# Revit family: RHTG1025
name_source: partatom
category: Windows
units: mm (PartAtom-declared; Revit-internal decimal feet)

## family parameters
Always vertical = No
Cut with Voids When Loaded = No
Host = Roof
Room Calculation Point = No
Shared = No

## types (4) — shared parameters
A = 1000 mm  [stored 3.28084 ft]
Analytic Construction = <None>
BEV L 1 = 400 mm  [stored 1.31234 ft]
BEV L 3 = 400 mm  [stored 1.31234 ft]
Define Thermal Properties by = Schematic Type
Geluidwerendheid = 27 dB
Hatch Material = Gorter
Manufacturer = Gorter
Model = RHTG
Oppervlaktebehandeling binnenzijde = Gepoedercoat RAL9010
Gepoedercoat in RAL7011 (buitenzijde) en RAL9010 (binnenzijde).
Gepoedercoat RAL 9010
Oppervlaktebehandeling buitenzijde = Gepoedercoat RAL9005 / RAL9010
Gepoedercoat in RAL7011 (buitenzijde) en RAL9010 (binnenzijde).
Gepoedercoat RAL 7011
Rough Width = 1000 mm  [stored 3.28084 ft]
URL = https://www.gortergroup.com
Width = 1000 mm  [stored 3.28084 ft]

## per-type parameters (varying)
| type | B | BEV L 2 | Height | Rough Height | Weight (kg) |
| RHTG1015 | 1500 mm  [stored 4.92126 ft] | 400 mm  [stored 1.31234 ft] | 1500 mm  [stored 4.92126 ft] | 1500 mm  [stored 4.92126 ft] | 173 |
| RHTG1025 | 2500 mm  [stored 8.2021 ft] | 800 mm  [stored 2.62467 ft] | 2500 mm  [stored 8.2021 ft] | 2500 mm  [stored 8.2021 ft] | 264 |
| RHTG1030 | 3000 mm  [stored 9.84252 ft] | 400 mm  [stored 1.31234 ft] | 3000 mm  [stored 9.84252 ft] | 3000 mm  [stored 9.84252 ft] | 309 |
| RHTG1020 | 2000 mm  [stored 6.56168 ft] | 400 mm  [stored 1.31234 ft] | 2000 mm  [stored 6.56168 ft] | 2000 mm  [stored 6.56168 ft] | 219 |

note: [stored X ft] marks values corroborated as IEEE doubles in the binary element streams (Revit-internal decimal feet)

## geometry (parser evidence)
native form markers: Sweep x1
no freeform markers — native parametric forms only
